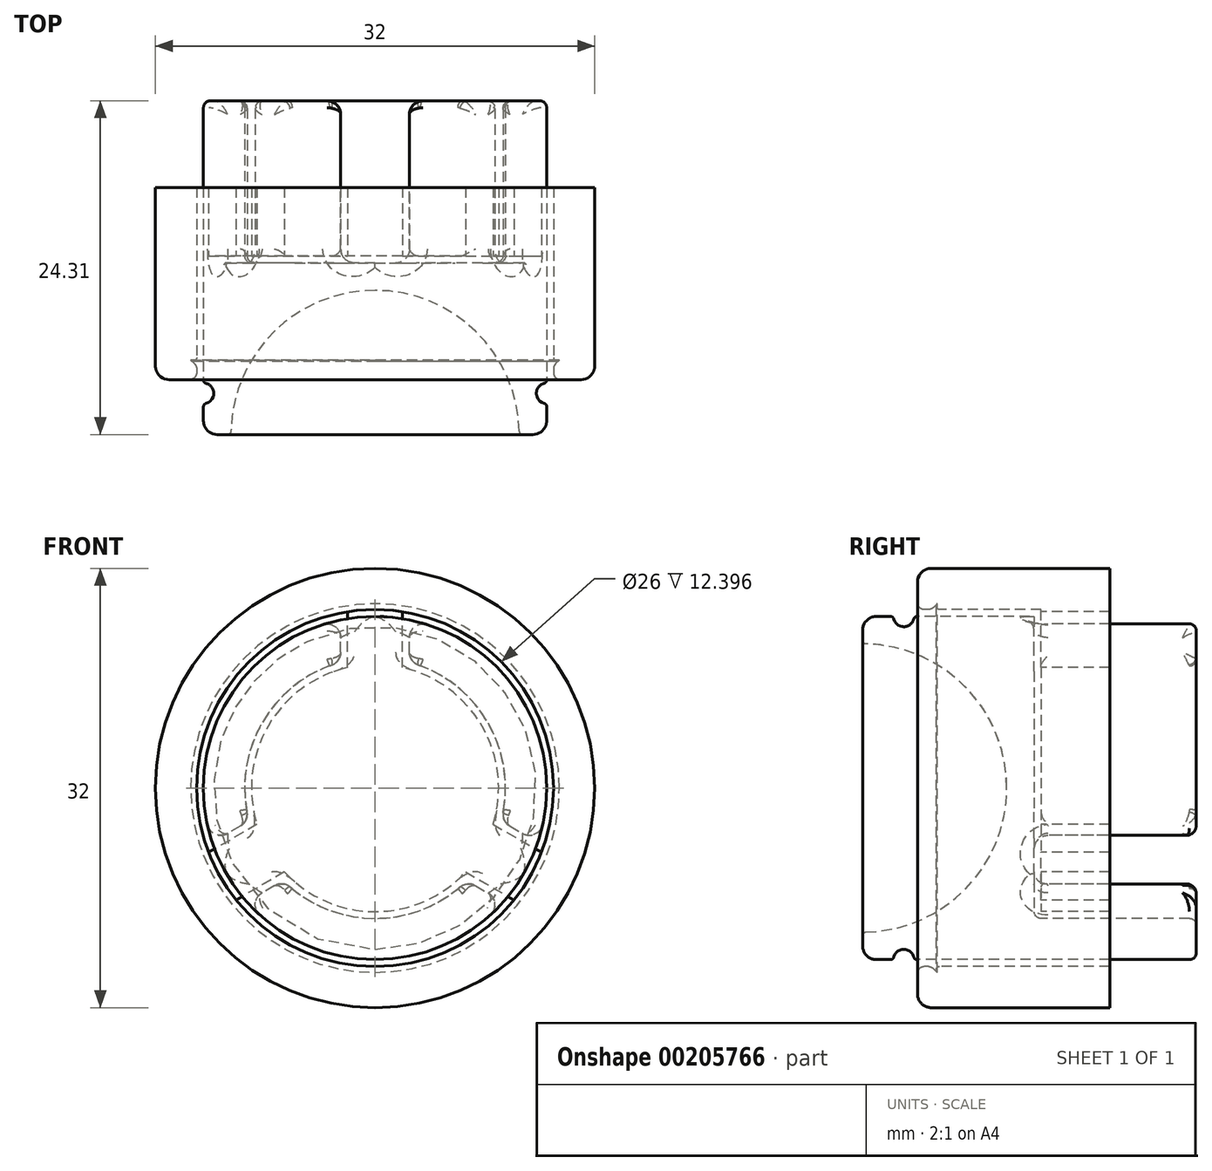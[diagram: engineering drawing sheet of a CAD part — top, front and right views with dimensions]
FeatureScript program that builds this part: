
annotation { "Feature Type Name" : "Feature", "Feature Type Description" : "" }
export const myFeature = defineFeature(function(context is Context, id is Id, definition is map)
    precondition{}
    {
        {
            var Q0;
            Q0=qCreatedBy(makeId("Right.planeOp"),FACE);
            var sketch = newSketch(context, id + "F0", { "sketchPlane" : qUnion([Q0])});
            skLineSegment(sketch, "E0", {"start": v(0, 0) * mm, "end": v(50, 0) * mm, "construction": true});
            skCircle(sketch, "E1", {"center": v(25, 0) * mm, "radius": 25 * mm});
            skCircle(sketch, "E2", {"center": v(25, 0) * mm, "radius": 23 * mm});
            skLineSegment(sketch, "E3", {"start": v(5.7, 12.5) * mm, "end": v(5.7, -12.5) * mm});
            skSolve(sketch);
        }
        {
            var Q0;
            Q0=qCreatedBy(makeId("Right.planeOp"),FACE);
            var sketch = newSketch(context, id + "F1", { "sketchPlane" : qUnion([Q0])});
            skArc(sketch, "E4", {"start": v(16.2, 0) * mm, "mid": v(13.2, 7.34) * mm, "end": v(5.94, 10.5) * mm});
            skLineSegment(sketch, "E5", {"start": v(5.7, 10.75) * mm, "end": v(5.7, 11.5) * mm});
            skLineSegment(sketch, "E6", {"start": v(6.7, 12.5) * mm, "end": v(7.73, 12.5) * mm});
            skLineSegment(sketch, "E7.0", {"start": v(0, 0) * mm, "end": v(50, 0) * mm, "construction": true});
            skPoint(sketch, "E8.visualSharp", {"position": v(5.7, 12.5) * mm});
            skArc(sketch, "E8.filletArc", {"start": v(6.7, 12.5) * mm, "mid": v(5.99, 12.2) * mm, "end": v(5.7, 11.5) * mm});
            skLineSegment(sketch, "E9", {"start": v(18.2, 0) * mm, "end": v(18.2, 9) * mm});
            skLineSegment(sketch, "E10", {"start": v(18.7, 9.5) * mm, "end": v(29.5, 9.5) * mm});
            skLineSegment(sketch, "E11", {"start": v(30, 10) * mm, "end": v(30, 12) * mm});
            skLineSegment(sketch, "E12", {"start": v(18.2, 0) * mm, "end": v(16.2, 0) * mm});
            skArc(sketch, "E13", {"start": v(7.97, 12.31) * mm, "mid": v(8.7, 11.75) * mm, "end": v(9.42, 12.31) * mm});
            skLineSegment(sketch, "E14.trimOffspring", {"start": v(9.66, 12.5) * mm, "end": v(29.5, 12.5) * mm});
            skPoint(sketch, "E15.visualSharp", {"position": v(7.94, 12.5) * mm});
            skArc(sketch, "E15.filletArc", {"start": v(7.97, 12.31) * mm, "mid": v(7.88, 12.45) * mm, "end": v(7.73, 12.5) * mm});
            skPoint(sketch, "E16.visualSharp", {"position": v(9.44, 12.5) * mm});
            skArc(sketch, "E16.filletArc", {"start": v(9.66, 12.5) * mm, "mid": v(9.5, 12.45) * mm, "end": v(9.42, 12.31) * mm});
            skPoint(sketch, "E17.visualSharp", {"position": v(5.7, 10.5) * mm});
            skArc(sketch, "E17.filletArc", {"start": v(5.7, 10.75) * mm, "mid": v(5.76, 10.57) * mm, "end": v(5.94, 10.5) * mm});
            skPoint(sketch, "E18.visualSharp", {"position": v(30, 9.5) * mm});
            skArc(sketch, "E18.filletArc", {"start": v(29.5, 9.5) * mm, "mid": v(29.85, 9.65) * mm, "end": v(30, 10) * mm});
            skPoint(sketch, "E19.visualSharp", {"position": v(30, 12.5) * mm});
            skArc(sketch, "E19.filletArc", {"start": v(30, 12) * mm, "mid": v(29.85, 12.35) * mm, "end": v(29.5, 12.5) * mm});
            skPoint(sketch, "E20.visualSharp", {"position": v(18.2, 9.5) * mm});
            skArc(sketch, "E20.filletArc", {"start": v(18.7, 9.5) * mm, "mid": v(18.34, 9.35) * mm, "end": v(18.2, 9) * mm});
            skSolve(sketch);
        }
        {
            var Q0;
            Q0 = qSketchRegion(id + "F1", true);
            var Q1;
            Q1=sQuery(id+"F0.wireOp",EDGE,"E0");
            revolve(context, id + "F2", {"entities" : qUnion([Q0]), "axis" : qUnion([Q1]), "revolveType" : RevolveType.FULL});
        }
        {
            var Q0;
            Q0=qCreatedBy(makeId("Right.planeOp"),FACE);
            var sketch = newSketch(context, id + "F3", { "sketchPlane" : qUnion([Q0])});
            skLineSegment(sketch, "E21", {"start": v(9.7, 13) * mm, "end": v(10.7, 13) * mm});
            skLineSegment(sketch, "E22", {"start": v(10.7, 13) * mm, "end": v(13.7, 16) * mm});
            skLineSegment(sketch, "E23", {"start": v(13.7, 16) * mm, "end": v(17.7, 16) * mm});
            skLineSegment(sketch, "E24", {"start": v(17.7, 16) * mm, "end": v(17.7, 13) * mm});
            skLineSegment(sketch, "E25", {"start": v(17.7, 13) * mm, "end": v(10.7, 13) * mm});
            skLineSegment(sketch, "E26", {"start": v(13.7, 16) * mm, "end": v(9.7, 16) * mm});
            skLineSegment(sketch, "E27", {"start": v(9.7, 16) * mm, "end": v(9.7, 13) * mm});
            skSolve(sketch);
        }
        {
            var Q0;
            Q0=qCreatedBy(makeId("Right.planeOp"),FACE);
            var sketch = newSketch(context, id + "F4", { "sketchPlane" : qUnion([Q0])});
            skLineSegment(sketch, "E28.0", {"start": v(13.09, 16) * mm, "end": v(10.7, 16) * mm});
            skLineSegment(sketch, "E28.1", {"start": v(9.7, 15) * mm, "end": v(9.7, 13.5) * mm});
            skLineSegment(sketch, "E28.2", {"start": v(10.2, 13) * mm, "end": v(10.49, 13) * mm});
            skLineSegment(sketch, "E28.3", {"start": v(10.84, 13.15) * mm, "end": v(13.27, 15.57) * mm});
            skPoint(sketch, "E29.visualSharp", {"position": v(9.7, 13) * mm});
            skArc(sketch, "E29.filletArc", {"start": v(9.7, 13.5) * mm, "mid": v(9.84, 13.15) * mm, "end": v(10.2, 13) * mm});
            skPoint(sketch, "E30.visualSharp", {"position": v(10.7, 13) * mm});
            skArc(sketch, "E30.filletArc", {"start": v(10.49, 13) * mm, "mid": v(10.68, 13.04) * mm, "end": v(10.84, 13.15) * mm});
            skPoint(sketch, "E31.visualSharp", {"position": v(9.7, 16) * mm});
            skArc(sketch, "E31.filletArc", {"start": v(10.7, 16) * mm, "mid": v(9.99, 15.7) * mm, "end": v(9.7, 15) * mm});
            skPoint(sketch, "E32.visualSharp", {"position": v(13.7, 16) * mm});
            skArc(sketch, "E32.filletArc", {"start": v(13.27, 15.57) * mm, "mid": v(13.32, 15.85) * mm, "end": v(13.09, 16) * mm});
            skLineSegment(sketch, "E33.0", {"start": v(0, 0) * mm, "end": v(50, 0) * mm, "construction": true});
            skSolve(sketch);
        }
        {
            var Q0;
            Q0 = qSketchRegion(id + "F4", true);
            var Q1;
            Q1=sQuery(id+"F0.wireOp",EDGE,"E0");
            revolve(context, id + "F5", {"entities" : qUnion([Q0]), "axis" : qUnion([Q1]), "revolveType" : RevolveType.FULL});
        }
        {
            var Q0;
            Q0=qCreatedBy(makeId("Right.planeOp"),FACE);
            var sketch = newSketch(context, id + "F6", { "sketchPlane" : qUnion([Q0])});
            skLineSegment(sketch, "E34.0", {"start": v(13.9, 16) * mm, "end": v(16.7, 16) * mm});
            skLineSegment(sketch, "E34.1", {"start": v(17.7, 15) * mm, "end": v(17.7, 13) * mm});
            skLineSegment(sketch, "E34.2", {"start": v(17.7, 13) * mm, "end": v(11.3, 13) * mm});
            skLineSegment(sketch, "E34.3", {"start": v(11.12, 13.43) * mm, "end": v(13.55, 15.85) * mm});
            skPoint(sketch, "E35.visualSharp", {"position": v(10.7, 13) * mm});
            skArc(sketch, "E35.filletArc", {"start": v(11.12, 13.43) * mm, "mid": v(11.07, 13.15) * mm, "end": v(11.3, 13) * mm});
            skPoint(sketch, "E36.visualSharp", {"position": v(13.7, 16) * mm});
            skArc(sketch, "E36.filletArc", {"start": v(13.9, 16) * mm, "mid": v(13.7, 15.96) * mm, "end": v(13.55, 15.85) * mm});
            skPoint(sketch, "E37.visualSharp", {"position": v(17.7, 16) * mm});
            skArc(sketch, "E37.filletArc", {"start": v(17.7, 15) * mm, "mid": v(17.4, 15.7) * mm, "end": v(16.7, 16) * mm});
            skSolve(sketch);
        }
        {
            var Q0;
            Q0 = qSketchRegion(id + "F6", true);
            var Q1;
            Q1=sQuery(id+"F6.wireOp",EDGE,"E34.1");
            var Q2;
            Q2=sQuery(id+"F0.wireOp",EDGE,"E0");
            revolve(context, id + "F7", {"entities" : qUnion([Q0]), "surfaceEntities" : qUnion([Q1]), "axis" : qUnion([Q2]), "revolveType" : RevolveType.FULL});
        }
        {
            var Q0;
            Q0=sQuery(id+"F1.wireOp",VERTEX,"E12.start");
            var Q1;
            Q1=qCreatedBy(makeId("Front.planeOp"),FACE);
            cPlane(context, id + "F8", {"entities" : qUnion([Q0, Q1]), "cplaneType" : CPlaneType.PLANE_POINT, "offset" : 20 * mm, "oppositeDirection" : true, "width" : 150 * mm, "height" : 150 * mm});
        }
        {
            var Q0;
            Q0=qCreatedBy(id+"F8.planeOp",FACE);
            var sketch = newSketch(context, id + "F9", { "sketchPlane" : qUnion([Q0])});
            skCircle(sketch, "E38", {"center": v(0, 0) * mm, "radius": 9 * mm});
            skPoint(sketch, "E39", {"position": v(0, 9) * mm});
            skLineSegment(sketch, "E40", {"start": v(0, 9) * mm, "end": v(0, 13) * mm, "construction": true});
            skLineSegment(sketch, "E41", {"start": v(2.5, 8.65) * mm, "end": v(2.5, 13) * mm});
            skLineSegment(sketch, "E42", {"start": v(2.5, 13) * mm, "end": v(0, 13) * mm});
            skLineSegment(sketch, "E43.MirrorCS", {"start": v(-2.5, 8.65) * mm, "end": v(-2.5, 13) * mm});
            skLineSegment(sketch, "E44.MirrorCS", {"start": v(-2.5, 13) * mm, "end": v(0, 13) * mm});
            skLineSegment(sketch, "E45.1.0", {"start": v(-6.24, -6.49) * mm, "end": v(-10, -8.67) * mm});
            skLineSegment(sketch, "E45.1.1", {"start": v(-12.5, -4.33) * mm, "end": v(-11.26, -6.5) * mm});
            skLineSegment(sketch, "E45.1.2", {"start": v(-10, -8.67) * mm, "end": v(-11.26, -6.5) * mm});
            skLineSegment(sketch, "E45.1.3", {"start": v(-8.74, -2.16) * mm, "end": v(-12.5, -4.33) * mm});
            skLineSegment(sketch, "E45.2.0", {"start": v(8.74, -2.16) * mm, "end": v(12.5, -4.33) * mm});
            skLineSegment(sketch, "E45.2.1", {"start": v(10, -8.67) * mm, "end": v(11.26, -6.5) * mm});
            skLineSegment(sketch, "E45.2.2", {"start": v(12.5, -4.33) * mm, "end": v(11.26, -6.5) * mm});
            skLineSegment(sketch, "E45.2.3", {"start": v(6.24, -6.49) * mm, "end": v(10, -8.67) * mm});
            skSolve(sketch);
        }
        {
            var Q0;
            {var subQ0=sQuery(id+"F9.wireOp",EDGE,"E45.2.0");Q0=makeQuery(id+"F9.imprint","IMPRINT",FACE,{"disambiguationData":[TD([[makeQuery(id+"F9.imprint","IMPRINT",EDGE,{"derivedFrom":subQ0}),-1.0]])]});}
            var Q1;
            {var subQ0=sQuery(id+"F9.wireOp",EDGE,"E45.1.0");Q1=makeQuery(id+"F9.imprint","IMPRINT",FACE,{"disambiguationData":[TD([[makeQuery(id+"F9.imprint","IMPRINT",EDGE,{"derivedFrom":subQ0}),-1.0]])]});}
            var Q2;
            {var subQ1=sQuery(id+"F9.wireOp",EDGE,"E41");Q2=makeQuery(id+"F9.imprint","IMPRINT",FACE,{"disambiguationData":[TD([[makeQuery(id+"F9.imprint","IMPRINT",EDGE,{"derivedFrom":subQ1}),1.0]])]});}
            extrude(context, id + "F10", {"entities" : qUnion([Q0, Q1, Q2]), "operationType" : NewBodyOperationType.REMOVE, "endBound" : BoundingType.THROUGH_ALL, "oppositeDirection" : true, "depth" : 10 * mm});
        }
        {
            var Q0;
            {var subQ0=sQuery(id+"F9.wireOp",EDGE,"E38");Q0=makeQuery(id+"F10.boolean.opBoolean","MERGE",FACE,{"derivedFrom":[makeQuery(id+"F2.opRevolve","SWEPT_FACE",FACE,{"disambiguationData":[OSD([sQuery(id+"F1.wireOp",EDGE,"E9")])]}),makeQuery(id+"F10.opExtrude","CAP_FACE",FACE,{"disambiguationData":[OSD([subQ0,sQuery(id+"F9.wireOp",EDGE,"E41"),sQuery(id+"F9.wireOp",EDGE,"E42"),sQuery(id+"F9.wireOp",EDGE,"E43.MirrorCS"),sQuery(id+"F9.wireOp",EDGE,"E44.MirrorCS")])],"isStart":true}),makeQuery(id+"F10.opExtrude","CAP_FACE",FACE,{"disambiguationData":[OSD([subQ0,sQuery(id+"F9.wireOp",EDGE,"E45.1.0"),sQuery(id+"F9.wireOp",EDGE,"E45.1.1"),sQuery(id+"F9.wireOp",EDGE,"E45.1.2"),sQuery(id+"F9.wireOp",EDGE,"E45.1.3")])],"isStart":true}),makeQuery(id+"F10.opExtrude","CAP_FACE",FACE,{"disambiguationData":[OSD([subQ0,sQuery(id+"F9.wireOp",EDGE,"E45.2.0"),sQuery(id+"F9.wireOp",EDGE,"E45.2.1"),sQuery(id+"F9.wireOp",EDGE,"E45.2.2"),sQuery(id+"F9.wireOp",EDGE,"E45.2.3")])],"isStart":true})]});}
            cPlane(context, id + "F11", {"entities" : qUnion([Q0]), "cplaneType" : CPlaneType.OFFSET, "offset" : .5 * mm, "width" : 150 * mm, "height" : 150 * mm});
        }
        {
            var Q0;
            Q0=qCreatedBy(id+"F11.planeOp",FACE);
            var sketch = newSketch(context, id + "F12", { "sketchPlane" : qUnion([Q0])});
            skLineSegment(sketch, "E46.0", {"start": v(-2, 8.77) * mm, "end": v(-2, 12.85) * mm});
            skLineSegment(sketch, "E47.0", {"start": v(2, 8.77) * mm, "end": v(2, 12.85) * mm});
            skArc(sketch, "E48.0", {"start": v(2, 8.77) * mm, "mid": v(7.8, 4.5) * mm, "end": v(8.6, -2.66) * mm});
            skArc(sketch, "E49", {"start": v(-10.12, -8.15) * mm, "mid": v(0, -13) * mm, "end": v(10.12, -8.15) * mm});
            skCircle(sketch, "E50", {"center": v(0, 0) * mm, "radius": 16 * mm});
            skLineSegment(sketch, "E51.1.0", {"start": v(-8.6, -2.66) * mm, "end": v(-12.12, -4.7) * mm});
            skLineSegment(sketch, "E51.1.1", {"start": v(-6.6, -6.12) * mm, "end": v(-10.12, -8.15) * mm});
            skLineSegment(sketch, "E51.2.0", {"start": v(6.6, -6.12) * mm, "end": v(10.12, -8.15) * mm});
            skLineSegment(sketch, "E51.2.1", {"start": v(8.6, -2.66) * mm, "end": v(12.12, -4.7) * mm});
            skArc(sketch, "E52.trimOffspring", {"start": v(-8.6, -2.66) * mm, "mid": v(-7.8, 4.5) * mm, "end": v(-2, 8.77) * mm});
            skArc(sketch, "E53.trimOffspring", {"start": v(-2, 12.85) * mm, "mid": v(-11.26, 6.5) * mm, "end": v(-12.12, -4.7) * mm});
            skArc(sketch, "E54.trimOffspring", {"start": v(12.12, -4.7) * mm, "mid": v(11.26, 6.5) * mm, "end": v(2, 12.85) * mm});
            skArc(sketch, "E55.trimOffspring", {"start": v(6.6, -6.12) * mm, "mid": v(0, -9) * mm, "end": v(-6.6, -6.12) * mm});
            skSolve(sketch);
        }
        {
            var Q0;
            Q0 = qSketchRegion(id + "F12", true);
            extrude(context, id + "F13", {"entities" : qUnion([Q0]), "depth" : 5 * mm});
        }
        {
            var Q0;
            Q0=makeQuery(id+"F13.opExtrude","CAP_FACE",FACE,{"disambiguationData":[OSD([sQuery(id+"F12.wireOp",EDGE,"E46.0"),sQuery(id+"F12.wireOp",EDGE,"E47.0"),sQuery(id+"F12.wireOp",EDGE,"E48.0"),sQuery(id+"F12.wireOp",EDGE,"E49"),sQuery(id+"F12.wireOp",EDGE,"E50"),sQuery(id+"F12.wireOp",EDGE,"E51.1.0"),sQuery(id+"F12.wireOp",EDGE,"E51.1.1"),sQuery(id+"F12.wireOp",EDGE,"E51.2.0"),sQuery(id+"F12.wireOp",EDGE,"E51.2.1"),sQuery(id+"F12.wireOp",EDGE,"E52.trimOffspring"),sQuery(id+"F12.wireOp",EDGE,"E53.trimOffspring"),sQuery(id+"F12.wireOp",EDGE,"E54.trimOffspring"),sQuery(id+"F12.wireOp",EDGE,"E55.trimOffspring")])],"isStart":true});
            var sketch = newSketch(context, id + "F14", { "sketchPlane" : qUnion([Q0])});
            skCircle(sketch, "E56.0", {"center": v(0, 0) * mm, "radius": 16 * mm});
            skCircle(sketch, "E57", {"center": v(0, 0) * mm, "radius": 13 * mm});
            skSolve(sketch);
        }
        {
            var Q0;
            Q0 = qSketchRegion(id + "F14", true);
            extrude(context, id + "F15", {"entities" : qUnion([Q0]), "operationType" : NewBodyOperationType.ADD, "depth" : 6 * mm});
        }
        {
            var Q0;
            Q0=makeQuery(id+"F10.boolean.opBoolean","COPY",FACE,{"derivedFrom":makeQuery(id+"F10.opExtrude","SWEPT_FACE",FACE,{"disambiguationData":[OSD([sQuery(id+"F9.wireOp",EDGE,"E45.2.3")])]})});
            var Q1;
            Q1=makeQuery(id+"F10.boolean.opBoolean","COPY",FACE,{"derivedFrom":makeQuery(id+"F10.opExtrude","SWEPT_FACE",FACE,{"disambiguationData":[OSD([sQuery(id+"F9.wireOp",EDGE,"E45.2.0")])]})});
            var Q2;
            Q2=makeQuery(id+"F10.boolean.opBoolean","COPY",FACE,{"derivedFrom":makeQuery(id+"F10.opExtrude","SWEPT_FACE",FACE,{"disambiguationData":[OSD([sQuery(id+"F9.wireOp",EDGE,"E45.1.3")])]})});
            var Q3;
            Q3=makeQuery(id+"F10.boolean.opBoolean","COPY",FACE,{"derivedFrom":makeQuery(id+"F10.opExtrude","SWEPT_FACE",FACE,{"disambiguationData":[OSD([sQuery(id+"F9.wireOp",EDGE,"E45.1.0")])]})});
            var Q4;
            Q4=makeQuery(id+"F10.boolean.opBoolean","COPY",FACE,{"derivedFrom":makeQuery(id+"F10.opExtrude","SWEPT_FACE",FACE,{"disambiguationData":[OSD([sQuery(id+"F9.wireOp",EDGE,"E41")])]})});
            var Q5;
            Q5=makeQuery(id+"F10.boolean.opBoolean","COPY",FACE,{"derivedFrom":makeQuery(id+"F10.opExtrude","SWEPT_FACE",FACE,{"disambiguationData":[OSD([sQuery(id+"F9.wireOp",EDGE,"E43.MirrorCS")])]})});
            fillet(context, id + "F16", {"entities" : qUnion([Q0, Q1, Q2, Q3, Q4, Q5]), "radius" : 1 * mm, "tangentPropagation" : true, "allowEdgeOverflow" : false});
        }
    });
